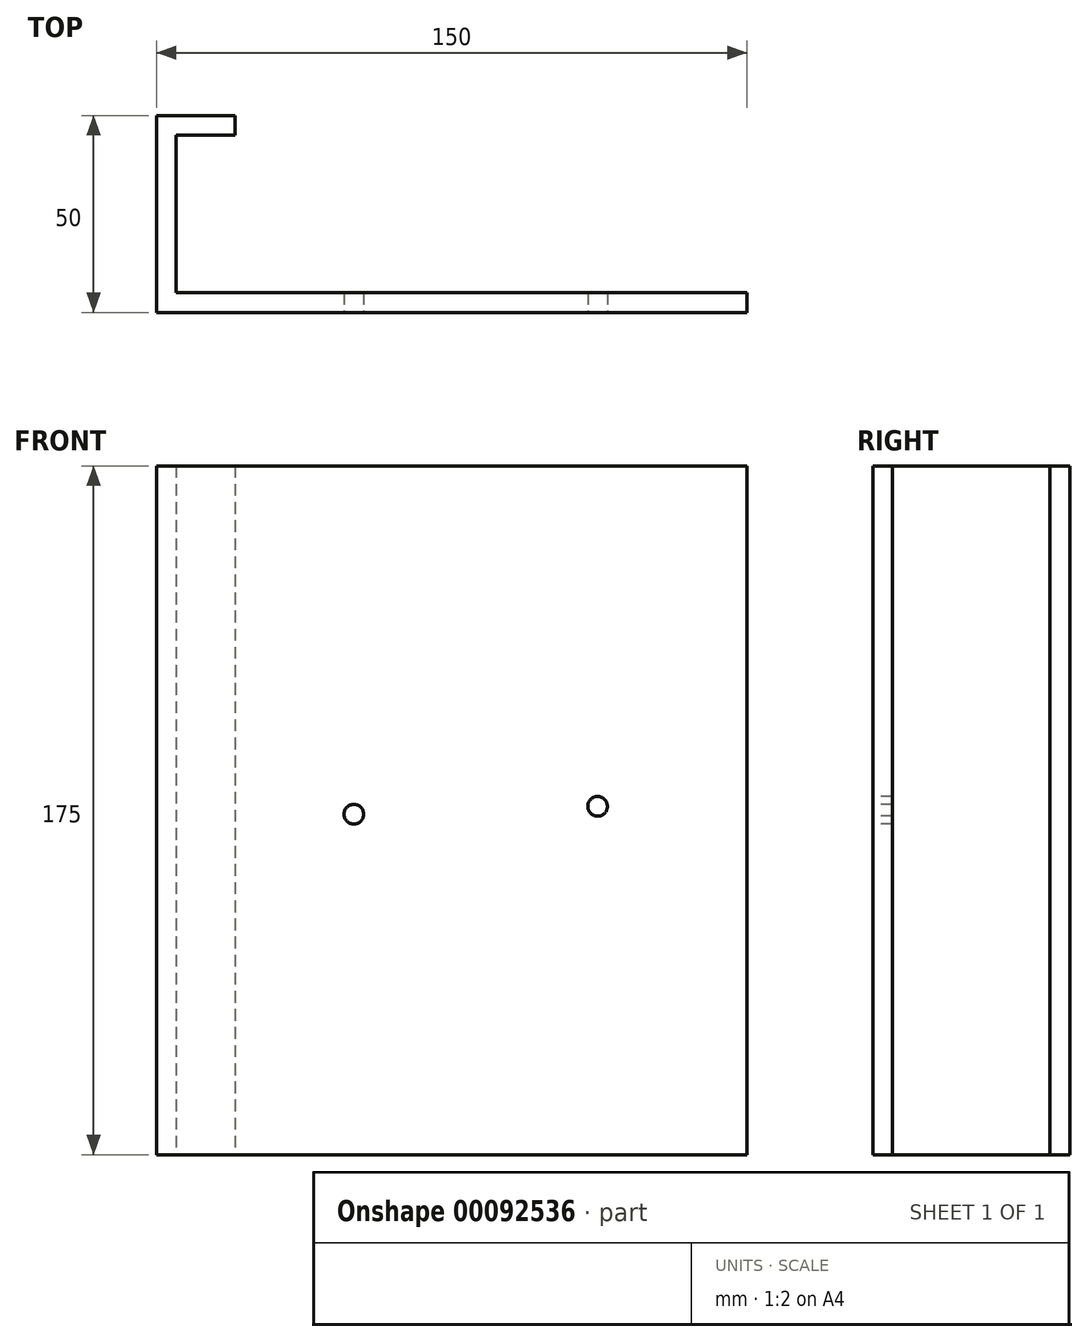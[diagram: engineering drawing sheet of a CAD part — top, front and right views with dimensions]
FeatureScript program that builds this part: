
annotation { "Feature Type Name" : "Feature", "Feature Type Description" : "" }
export const myFeature = defineFeature(function(context is Context, id is Id, definition is map)
    precondition{}
    {
        {
            var Q0;
            Q0=qCreatedBy(makeId("Top.planeOp"),FACE);
            var sketch = newSketch(context, id + "F0", { "sketchPlane" : qUnion([Q0])});
            skLineSegment(sketch, "E0", {"start": v(-112.04, -7.59) * mm, "end": v(37.96, -7.59) * mm});
            skLineSegment(sketch, "E1", {"start": v(-112.04, -7.59) * mm, "end": v(-112.04, 42.41) * mm});
            skLineSegment(sketch, "E2", {"start": v(-112.04, 42.41) * mm, "end": v(-92.04, 42.41) * mm});
            skLineSegment(sketch, "E3", {"start": v(-92.04, 42.41) * mm, "end": v(-92.04, 37.41) * mm});
            skLineSegment(sketch, "E4", {"start": v(-92.04, 37.41) * mm, "end": v(-107.04, 37.41) * mm});
            skLineSegment(sketch, "E5", {"start": v(-107.04, 37.41) * mm, "end": v(-107.04, -2.59) * mm});
            skLineSegment(sketch, "E6", {"start": v(-107.04, -2.59) * mm, "end": v(37.96, -2.59) * mm});
            skLineSegment(sketch, "E7", {"start": v(37.96, -2.59) * mm, "end": v(37.96, -7.59) * mm});
            skLineSegment(sketch, "E8", {"start": v(-112.04, 17.41) * mm, "end": v(-107.04, 17.41) * mm});
            skSolve(sketch);
        }
        {
            var Q0;
            Q0 = qSketchRegion(id + "F0", true);
            extrude(context, id + "F1", {"entities" : qUnion([Q0]), "depth" : 175 * mm});
        }
        {
            var Q0;
            Q0=makeQuery(id+"F1.opExtrude","SWEPT_FACE",FACE,{"disambiguationData":[OSD([sQuery(id+"F0.wireOp",EDGE,"E0")])]});
            var sketch = newSketch(context, id + "F2", { "sketchPlane" : qUnion([Q0])});
            skCircle(sketch, "E9", {"center": v(0, 88.5) * mm, "radius": 2.5 * mm});
            skCircle(sketch, "E10", {"center": v(-61.93, 86.5) * mm, "radius": 2.5 * mm});
            skLineSegment(sketch, "E11", {"start": v(0, 88.5) * mm, "end": v(0, 175) * mm});
            skLineSegment(sketch, "E12", {"start": v(0, 88.5) * mm, "end": v(37.96, 88.5) * mm});
            skLineSegment(sketch, "E13", {"start": v(-61.93, 86.5) * mm, "end": v(37.96, 91.38) * mm});
            skLineSegment(sketch, "E14", {"start": v(-61.93, 86.5) * mm, "end": v(-61.93, 0) * mm});
            skSolve(sketch);
        }
        {
            var Q0;
            Q0=makeQuery(id+"F2.imprint","IMPRINT",FACE,{"disambiguationData":[TD([[makeQuery(id+"F2.imprint","IMPRINT",EDGE,{"derivedFrom":sQuery(id+"F2.wireOp",EDGE,"E9")}),1.0]])]});
            extrude(context, id + "F3", {"entities" : qUnion([Q0]), "operationType" : NewBodyOperationType.REMOVE, "oppositeDirection" : true, "depth" : 25 * mm});
        }
        {
            var Q0;
            Q0 = qSketchRegion(id + "F2", true);
            extrude(context, id + "F4", {"entities" : qUnion([Q0]), "operationType" : NewBodyOperationType.REMOVE, "oppositeDirection" : true, "depth" : 25 * mm});
        }
    });
